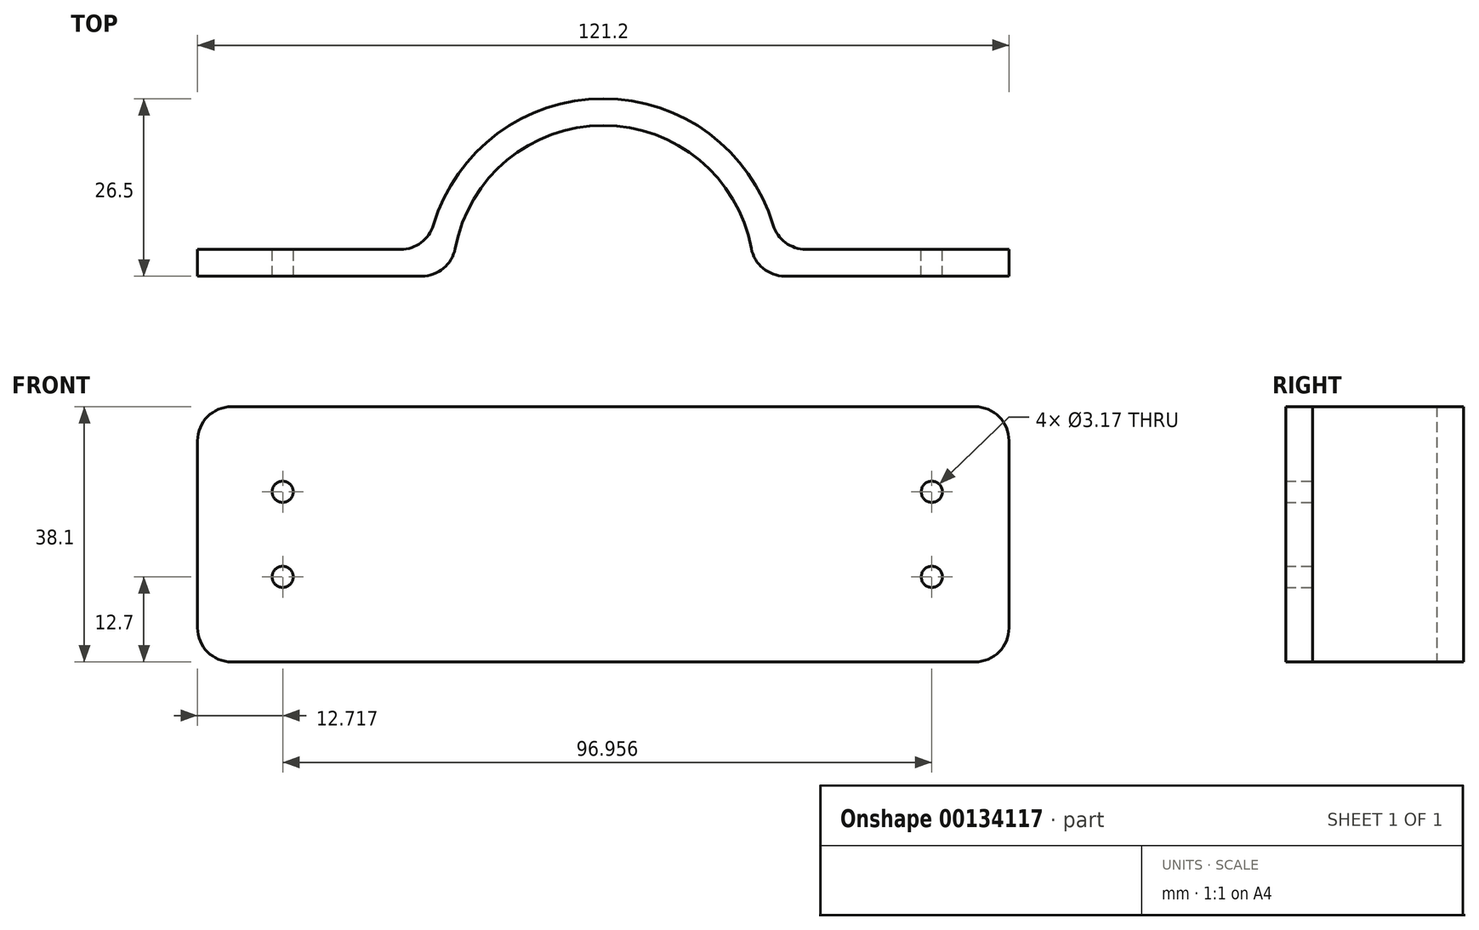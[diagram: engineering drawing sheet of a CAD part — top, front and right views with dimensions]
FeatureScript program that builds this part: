
annotation { "Feature Type Name" : "Feature", "Feature Type Description" : "" }
export const myFeature = defineFeature(function(context is Context, id is Id, definition is map)
    precondition{}
    {
        {
            var Q0;
            Q0=qCreatedBy(makeId("Top.planeOp"),FACE);
            var sketch = newSketch(context, id + "F0", { "sketchPlane" : qUnion([Q0])});
            skLineSegment(sketch, "E0.bottom", {"start": v(32.32, 1.7) * mm, "end": v(70.42, 1.7) * mm});
            skLineSegment(sketch, "E0.top", {"start": v(32.32, -2.3) * mm, "end": v(70.42, -2.3) * mm});
            skLineSegment(sketch, "E0.left", {"start": v(32.32, 1.7) * mm, "end": v(32.32, -2.3) * mm});
            skLineSegment(sketch, "E0.right", {"start": v(70.42, 1.7) * mm, "end": v(70.42, -2.3) * mm});
            skArc(sketch, "E1", {"start": v(32.32, -2.3) * mm, "mid": v(9.82, 20.2) * mm, "end": v(-12.68, -2.3) * mm});
            skArc(sketch, "E2", {"start": v(36.32, -2.3) * mm, "mid": v(9.82, 24.2) * mm, "end": v(-16.68, -2.3) * mm});
            skLineSegment(sketch, "E3.bottom", {"start": v(-12.68, -2.3) * mm, "end": v(-50.78, -2.3) * mm});
            skLineSegment(sketch, "E3.top", {"start": v(-12.68, 1.7) * mm, "end": v(-50.78, 1.7) * mm});
            skLineSegment(sketch, "E3.left", {"start": v(-12.68, -2.3) * mm, "end": v(-12.68, 1.7) * mm});
            skLineSegment(sketch, "E3.right", {"start": v(-50.78, -2.3) * mm, "end": v(-50.78, 1.7) * mm});
            skSolve(sketch);
        }
        {
            var Q0;
            Q0 = qSketchRegion(id + "F0", true);
            extrude(context, id + "F1", {"entities" : qUnion([Q0]), "depth" : 38.1 * mm});
        }
        {
            var Q0;
            Q0=makeQuery(id+"F1.opExtrude","CAP_EDGE",EDGE,{"disambiguationData":[OSD([sQuery(id+"F0.wireOp",EDGE,"E0.right")])],"isStart":false});
            var Q1;
            Q1=makeQuery(id+"F1.opExtrude","CAP_EDGE",EDGE,{"disambiguationData":[OSD([sQuery(id+"F0.wireOp",EDGE,"E0.right")])],"isStart":true});
            var Q2;
            Q2=makeQuery(id+"F1.opExtrude","SWEPT_EDGE",EDGE,{"disambiguationData":[OSD([sQuery(id+"F0.wireOp",EDGE,"E0.top"),sQuery(id+"F0.wireOp",EDGE,"E0.left"),sQuery(id+"F0.wireOp",EDGE,"E1")])]});
            var Q3;
            Q3=makeQuery(id+"F1.opExtrude","SWEPT_EDGE",EDGE,{"disambiguationData":[OSD([sQuery(id+"F0.wireOp",EDGE,"E1"),sQuery(id+"F0.wireOp",EDGE,"E3.bottom"),sQuery(id+"F0.wireOp",EDGE,"E3.left")])]});
            var Q4;
            Q4=makeQuery(id+"F1.opExtrude","CAP_EDGE",EDGE,{"disambiguationData":[OSD([sQuery(id+"F0.wireOp",EDGE,"E3.right")])],"isStart":false});
            var Q5;
            Q5=makeQuery(id+"F1.opExtrude","CAP_EDGE",EDGE,{"disambiguationData":[OSD([sQuery(id+"F0.wireOp",EDGE,"E3.right")])],"isStart":true});
            var Q6;
            Q6=makeQuery(id+"F1.opExtrude","SWEPT_EDGE",EDGE,{"disambiguationData":[OSD([sQuery(id+"F0.wireOp",EDGE,"E2"),sQuery(id+"F0.wireOp",EDGE,"E3.top")])]});
            var Q7;
            Q7=makeQuery(id+"F1.opExtrude","SWEPT_EDGE",EDGE,{"disambiguationData":[OSD([sQuery(id+"F0.wireOp",EDGE,"E0.bottom"),sQuery(id+"F0.wireOp",EDGE,"E2")])]});
            fillet(context, id + "F2", {"entities" : qUnion([Q0, Q1, Q2, Q3, Q4, Q5, Q6, Q7]), "radius" : 5.08 * mm, "tangentPropagation" : true, "allowEdgeOverflow" : false});
        }
        {
            var Q0;
            Q0=makeQuery(id+"F1.opExtrude","SWEPT_FACE",FACE,{"disambiguationData":[OSD([sQuery(id+"F0.wireOp",EDGE,"E0.bottom")])]});
            var sketch = newSketch(context, id + "F3", { "sketchPlane" : qUnion([Q0])});
            skPoint(sketch, "E4", {"position": v(-58.9, 12.7) * mm});
            skPoint(sketch, "E5", {"position": v(-58.9, 25.4) * mm});
            skPoint(sketch, "E6", {"position": v(38.06, 12.7) * mm});
            skPoint(sketch, "E7", {"position": v(38.06, 25.4) * mm});
            skSolve(sketch);
        }
        {
            var Q0;
            Q0=sQuery(id+"F3.wireOp",VERTEX,"E5");
            var Q1;
            Q1=sQuery(id+"F3.wireOp",VERTEX,"E4");
            var Q2;
            Q2=sQuery(id+"F3.wireOp",VERTEX,"E6");
            var Q3;
            Q3=sQuery(id+"F3.wireOp",VERTEX,"E7");
            var Q4;
            Q4=makeQuery(id+"F1.opExtrude","SWEPT_BODY",BODY,{"disambiguationData":[OSD([sQuery(id+"F0.wireOp",EDGE,"E0.bottom"),sQuery(id+"F0.wireOp",EDGE,"E0.top"),sQuery(id+"F0.wireOp",EDGE,"E0.right"),sQuery(id+"F0.wireOp",EDGE,"E1"),sQuery(id+"F0.wireOp",EDGE,"E2"),sQuery(id+"F0.wireOp",EDGE,"E3.bottom"),sQuery(id+"F0.wireOp",EDGE,"E3.top"),sQuery(id+"F0.wireOp",EDGE,"E3.right")])]});
            hole(context, id + "F4", {"style" : HoleStyle.SIMPLE, "endStyle" : HoleEndStyle.THROUGH, "holeDiameter" : 3.17 * mm, "locations" : qUnion([Q0, Q1, Q2, Q3]), "scope" : qUnion([Q4]), "isTappedThrough" : true});
        }
    });
